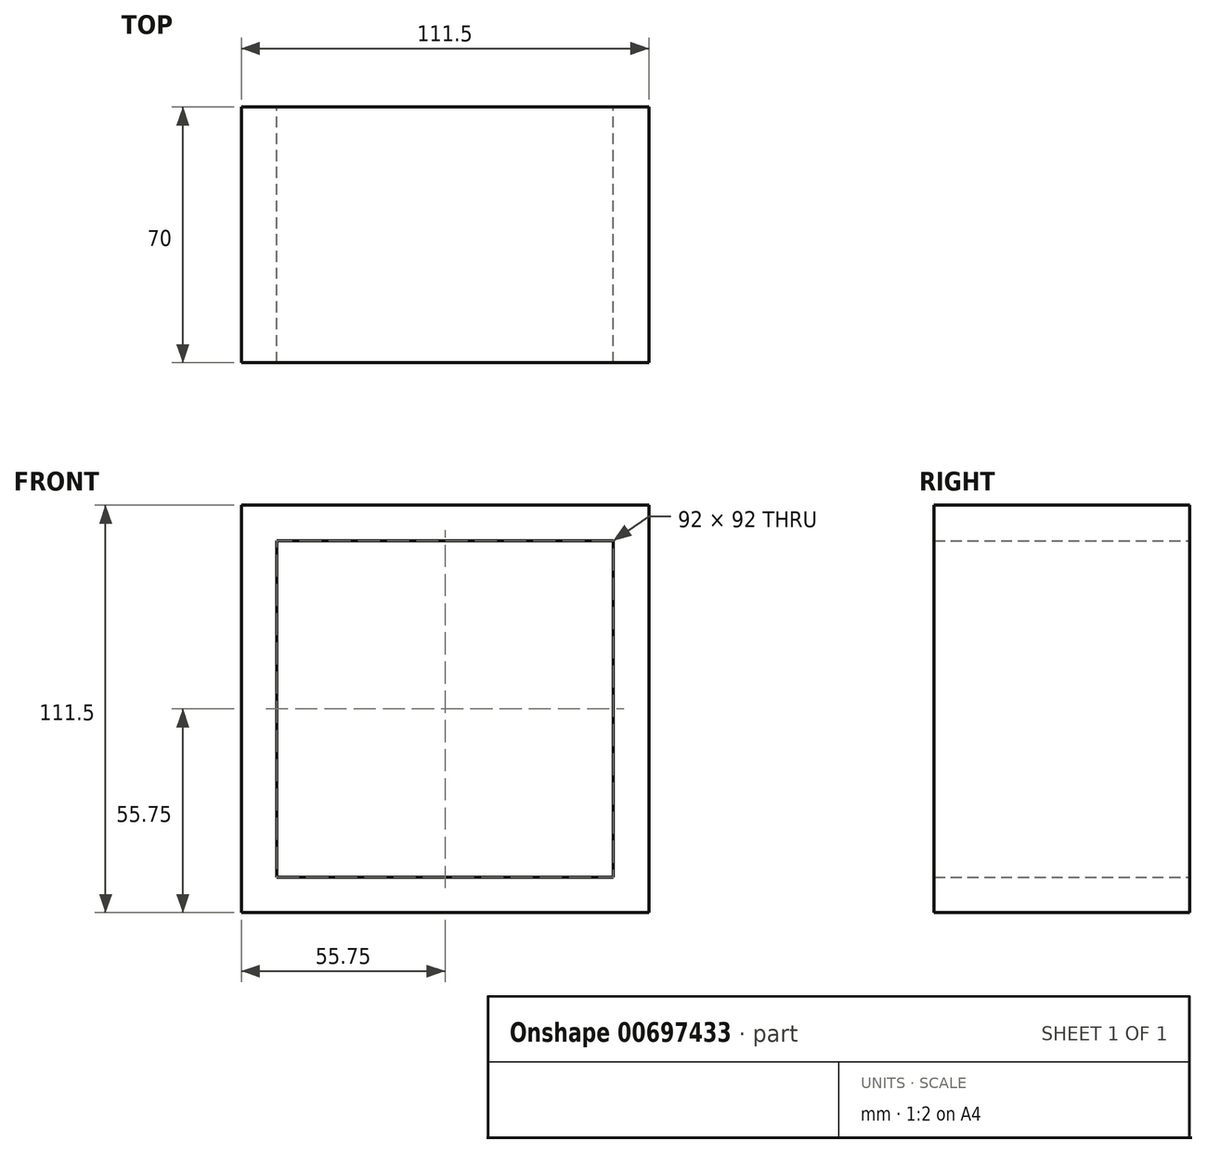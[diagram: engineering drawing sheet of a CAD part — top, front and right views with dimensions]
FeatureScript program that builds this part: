
annotation { "Feature Type Name" : "Feature", "Feature Type Description" : "" }
export const myFeature = defineFeature(function(context is Context, id is Id, definition is map)
    precondition{}
    {
        {
            var Q0;
            Q0=qCreatedBy(makeId("Front.planeOp"),FACE);
            var sketch = newSketch(context, id + "F0", { "sketchPlane" : qUnion([Q0])});
            skLineSegment(sketch, "E0.bottom", {"start": v(0, 0) * mm, "end": v(92, 0) * mm});
            skLineSegment(sketch, "E0.top", {"start": v(0, 92) * mm, "end": v(92, 92) * mm});
            skLineSegment(sketch, "E0.left", {"start": v(0, 0) * mm, "end": v(0, 92) * mm});
            skLineSegment(sketch, "E0.right", {"start": v(92, 0) * mm, "end": v(92, 92) * mm});
            skLineSegment(sketch, "E1.0", {"start": v(-9.75, 101.75) * mm, "end": v(101.75, 101.75) * mm});
            skLineSegment(sketch, "E1.1", {"start": v(-9.75, -9.75) * mm, "end": v(-9.75, 101.75) * mm});
            skLineSegment(sketch, "E1.2", {"start": v(-9.75, -9.75) * mm, "end": v(101.75, -9.75) * mm});
            skLineSegment(sketch, "E1.3", {"start": v(101.75, -9.75) * mm, "end": v(101.75, 101.75) * mm});
            skSolve(sketch);
        }
        {
            var Q0;
            Q0=makeQuery(id+"F0.imprint","IMPRINT",FACE,{"disambiguationData":[TD([[makeQuery(id+"F0.imprint","IMPRINT",EDGE,{"derivedFrom":sQuery(id+"F0.wireOp",EDGE,"E0.bottom")}),-1.0]])]});
            extrude(context, id + "F1", {"entities" : qUnion([Q0]), "depth" : 70 * mm, "offsetDistance" : 25 * mm});
        }
    });
